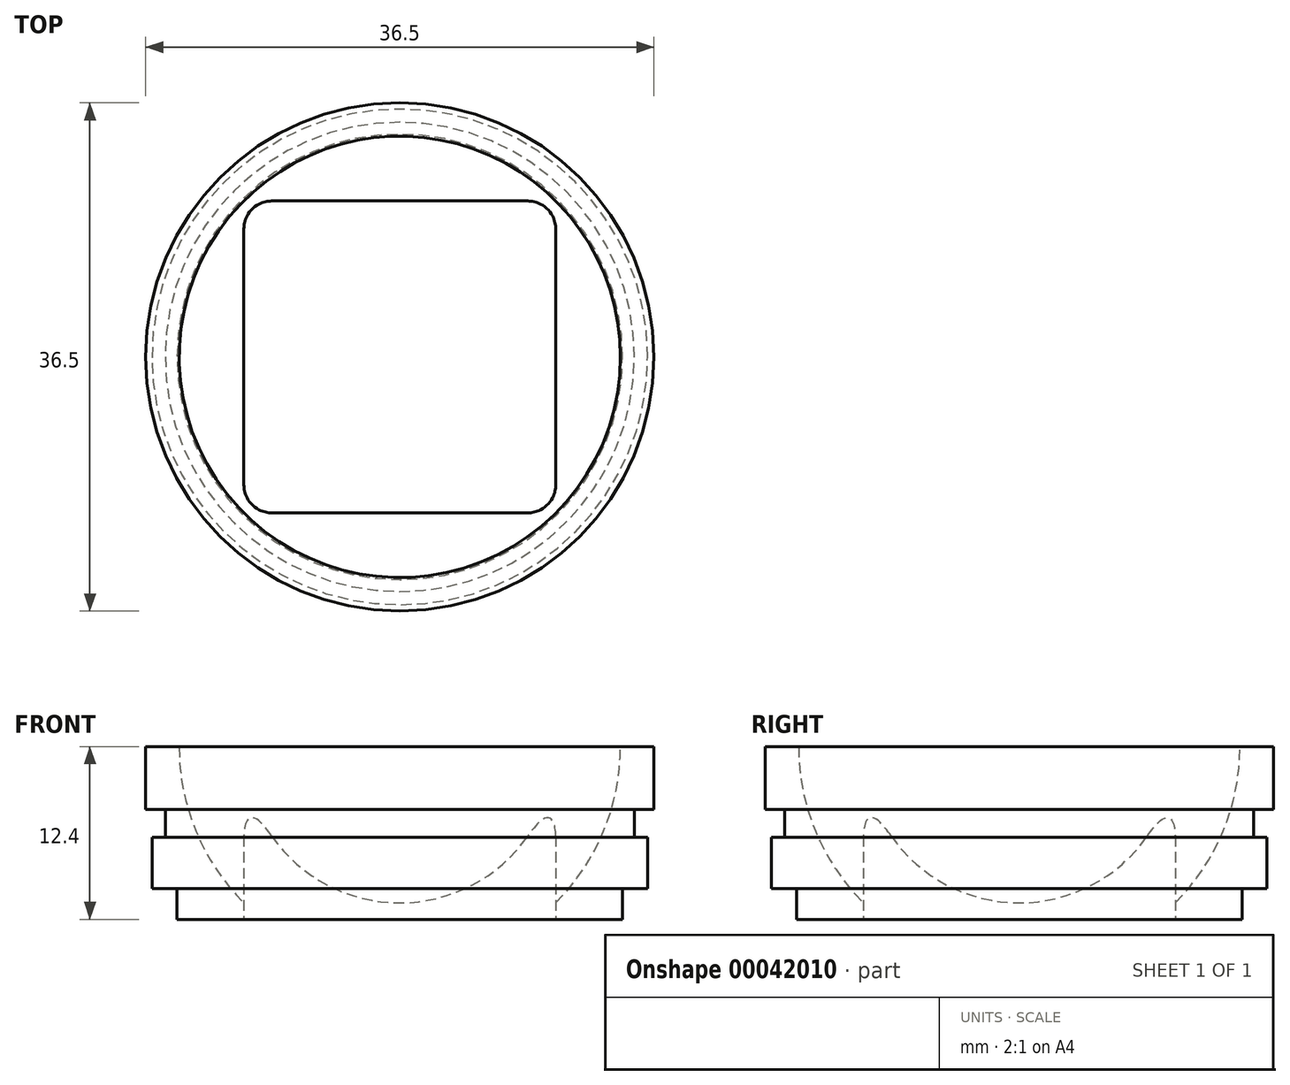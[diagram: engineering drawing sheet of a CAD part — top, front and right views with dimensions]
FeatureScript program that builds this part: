
annotation { "Feature Type Name" : "Feature", "Feature Type Description" : "" }
export const myFeature = defineFeature(function(context is Context, id is Id, definition is map)
    precondition{}
    {
        {
            var Q0;
            Q0=qCreatedBy(makeId("Top.planeOp"),FACE);
            var sketch = newSketch(context, id + "F0", { "sketchPlane" : qUnion([Q0])});
            skCircle(sketch, "E0", {"center": v(0, 0) * mm, "radius": 16 * mm});
            skSolve(sketch);
        }
        {
            var Q0;
            Q0 = qSketchRegion(id + "F0", true);
            extrude(context, id + "F1", {"entities" : qUnion([Q0]), "depth" : 2.2 * mm});
        }
        {
            var Q0;
            Q0=makeQuery(id+"F1.opExtrude","CAP_FACE",FACE,{"disambiguationData":[OSD([sQuery(id+"F0.wireOp",EDGE,"E0")])],"isStart":false});
            var sketch = newSketch(context, id + "F2", { "sketchPlane" : qUnion([Q0])});
            skCircle(sketch, "E1", {"center": v(0, 0) * mm, "radius": 17.8 * mm});
            skSolve(sketch);
        }
        {
            var Q0;
            Q0 = qSketchRegion(id + "F2", true);
            extrude(context, id + "F3", {"entities" : qUnion([Q0]), "operationType" : NewBodyOperationType.ADD, "depth" : 3.7 * mm});
        }
        {
            var Q0;
            Q0=makeQuery(id+"F3.opExtrude","CAP_FACE",FACE,{"disambiguationData":[OSD([sQuery(id+"F2.wireOp",EDGE,"E1")])],"isStart":false});
            var sketch = newSketch(context, id + "F4", { "sketchPlane" : qUnion([Q0])});
            skCircle(sketch, "E2", {"center": v(0, 0) * mm, "radius": 16.85 * mm});
            skSolve(sketch);
        }
        {
            var Q0;
            Q0 = qSketchRegion(id + "F4", true);
            extrude(context, id + "F5", {"entities" : qUnion([Q0]), "operationType" : NewBodyOperationType.ADD, "depth" : 2 * mm});
        }
        {
            var Q0;
            Q0=makeQuery(id+"F5.opExtrude","CAP_FACE",FACE,{"disambiguationData":[OSD([sQuery(id+"F4.wireOp",EDGE,"E2")])],"isStart":false});
            var sketch = newSketch(context, id + "F6", { "sketchPlane" : qUnion([Q0])});
            skCircle(sketch, "E3", {"center": v(0, 0) * mm, "radius": 18.25 * mm});
            skSolve(sketch);
        }
        {
            var Q0;
            Q0 = qSketchRegion(id + "F6", true);
            extrude(context, id + "F7", {"entities" : qUnion([Q0]), "operationType" : NewBodyOperationType.ADD, "depth" : 4.5 * mm});
        }
        {
            var Q0;
            Q0=makeQuery(id+"F1.opExtrude","CAP_FACE",FACE,{"disambiguationData":[OSD([sQuery(id+"F0.wireOp",EDGE,"E0")])],"isStart":true});
            var sketch = newSketch(context, id + "F8", { "sketchPlane" : qUnion([Q0])});
            skLineSegment(sketch, "E4", {"start": v(0, 0) * mm, "end": v(11.2, 0) * mm});
            skLineSegment(sketch, "E5", {"start": v(11.2, 0) * mm, "end": v(11.2, 11.2) * mm});
            skLineSegment(sketch, "E6.bottom", {"start": v(9.2, 11.2) * mm, "end": v(-9.2, 11.2) * mm});
            skLineSegment(sketch, "E6.top", {"start": v(9.2, -11.2) * mm, "end": v(-9.2, -11.2) * mm});
            skLineSegment(sketch, "E6.left", {"start": v(11.2, 9.2) * mm, "end": v(11.2, -9.2) * mm});
            skLineSegment(sketch, "E6.right", {"start": v(-11.2, 9.2) * mm, "end": v(-11.2, -9.2) * mm});
            skPoint(sketch, "E7.visualSharp", {"position": v(11.2, 11.2) * mm});
            skArc(sketch, "E7.filletArc", {"start": v(11.2, 9.2) * mm, "mid": v(10.61, 10.61) * mm, "end": v(9.2, 11.2) * mm});
            skPoint(sketch, "E8.visualSharp", {"position": v(-11.2, 11.2) * mm});
            skArc(sketch, "E8.filletArc", {"start": v(-9.2, 11.2) * mm, "mid": v(-10.61, 10.61) * mm, "end": v(-11.2, 9.2) * mm});
            skPoint(sketch, "E9.visualSharp", {"position": v(-11.2, -11.2) * mm});
            skArc(sketch, "E9.filletArc", {"start": v(-11.2, -9.2) * mm, "mid": v(-10.61, -10.61) * mm, "end": v(-9.2, -11.2) * mm});
            skPoint(sketch, "E10.visualSharp", {"position": v(11.2, -11.2) * mm});
            skArc(sketch, "E10.filletArc", {"start": v(9.2, -11.2) * mm, "mid": v(10.61, -10.61) * mm, "end": v(11.2, -9.2) * mm});
            skSolve(sketch);
        }
        {
            var Q0;
            Q0 = qSketchRegion(id + "F8", true);
            extrude(context, id + "F9", {"entities" : qUnion([Q0]), "operationType" : NewBodyOperationType.REMOVE, "endBound" : BoundingType.THROUGH_ALL, "oppositeDirection" : true, "depth" : 25 * mm});
        }
        {
            var Q0;
            Q0=qCreatedBy(makeId("Front.planeOp"),FACE);
            var sketch = newSketch(context, id + "F10", { "sketchPlane" : qUnion([Q0])});
            skLineSegment(sketch, "E11", {"start": v(0, 0) * mm, "end": v(0, 12.4) * mm});
            skCircle(sketch, "E12", {"center": v(0, 12.4) * mm, "radius": 15.85 * mm});
            skLineSegment(sketch, "E13", {"start": v(0, 0) * mm, "end": v(0, -3.45) * mm});
            skLineSegment(sketch, "E14", {"start": v(0, 12.4) * mm, "end": v(0, 28.25) * mm});
            skSolve(sketch);
        }
        {
            var Q0;
            Q0=makeQuery(id+"F10.imprint","IMPRINT",FACE,{"disambiguationData":[TD([[makeQuery(id+"F10.imprint","IMPRINT",EDGE,{"derivedFrom":sQuery(id+"F10.wireOp",EDGE,"E11")}),-1.0]])]});
            var Q1;
            Q1=sQuery(id+"F10.wireOp",EDGE,"E11");
            var Q2;
            Q2=sQuery(id+"F10.wireOp",EDGE,"E11");
            revolve(context, id + "F11", {"operationType" : NewBodyOperationType.REMOVE, "entities" : qUnion([Q0]), "surfaceEntities" : qUnion([Q1]), "axis" : qUnion([Q2]), "revolveType" : RevolveType.FULL, "oppositeDirection" : true});
        }
    });
